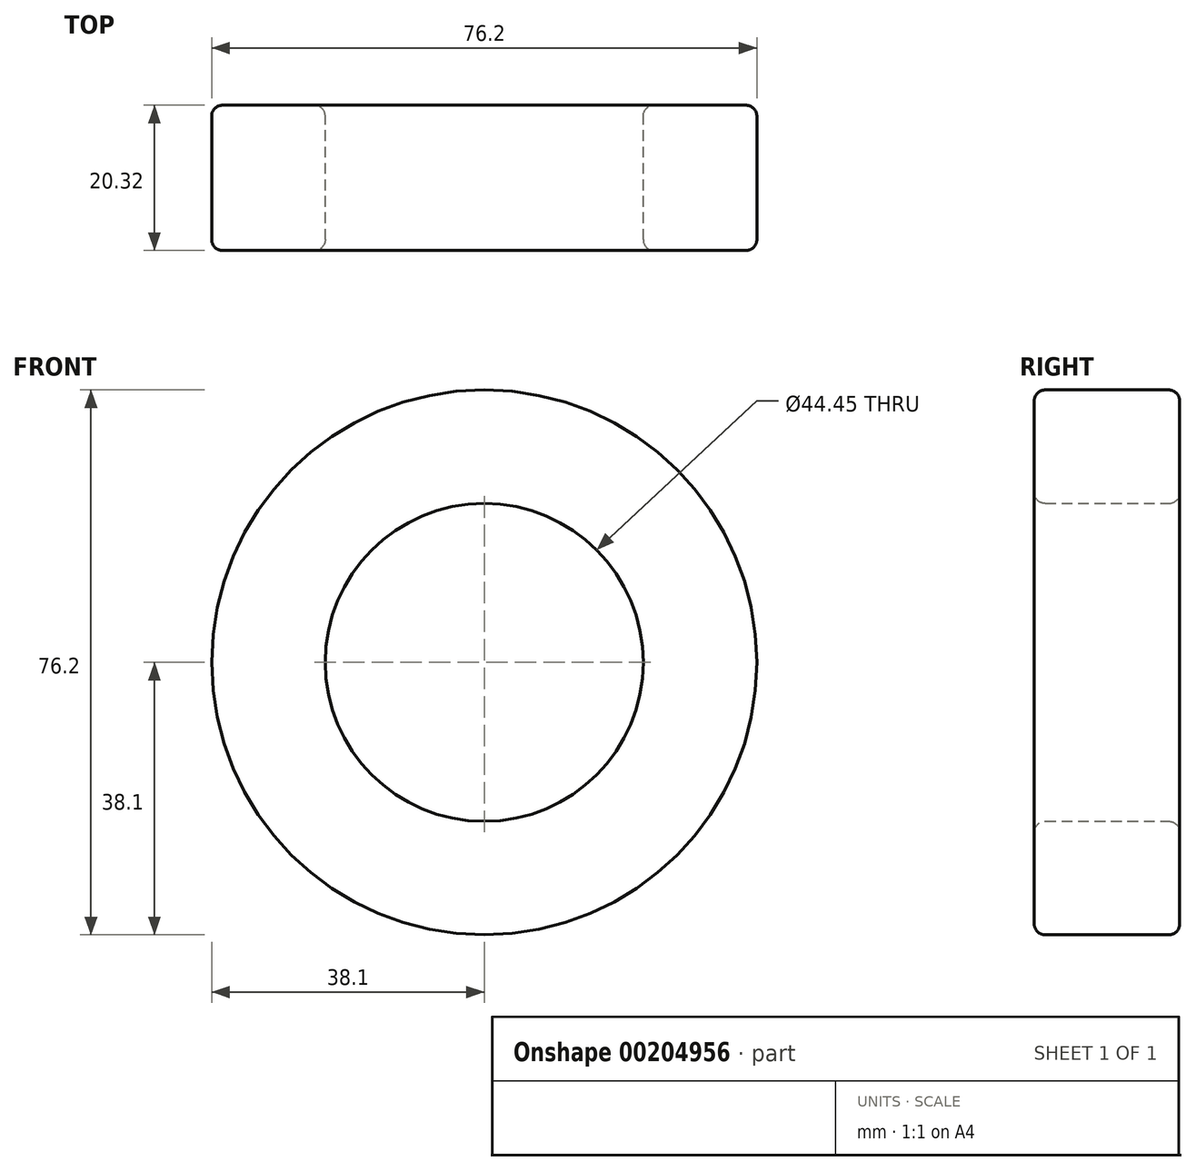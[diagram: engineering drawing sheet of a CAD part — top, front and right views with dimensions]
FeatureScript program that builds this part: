
annotation { "Feature Type Name" : "Feature", "Feature Type Description" : "" }
export const myFeature = defineFeature(function(context is Context, id is Id, definition is map)
    precondition{}
    {
        {
            var Q0;
            Q0=qCreatedBy(makeId("Front.planeOp"),FACE);
            var sketch = newSketch(context, id + "F0", { "sketchPlane" : qUnion([Q0])});
            skCircle(sketch, "E0", {"center": v(0, 0) * mm, "radius": 38.1 * mm});
            skCircle(sketch, "E1", {"center": v(0, 0) * mm, "radius": 22.23 * mm});
            skSolve(sketch);
        }
        {
            var Q0;
            Q0=makeQuery(id+"F0.imprint","IMPRINT",FACE,{"disambiguationData":[TD([[makeQuery(id+"F0.imprint","IMPRINT",EDGE,{"derivedFrom":sQuery(id+"F0.wireOp",EDGE,"E0")}),1.0]])]});
            extrude(context, id + "F1", {"entities" : qUnion([Q0]), "depth" : 20.32 * mm});
        }
        {
            var Q0;
            Q0=makeQuery(id+"F1.opExtrude","SWEPT_FACE",FACE,{"disambiguationData":[OSD([sQuery(id+"F0.wireOp",EDGE,"E0")])]});
            fillet(context, id + "F2", {"entities" : qUnion([Q0]), "radius" : 1.52 * mm, "tangentPropagation" : true, "allowEdgeOverflow" : false});
        }
        {
            var Q0;
            Q0=makeQuery(id+"F1.opExtrude","CAP_EDGE",EDGE,{"disambiguationData":[OSD([sQuery(id+"F0.wireOp",EDGE,"E1")])],"isStart":false});
            fillet(context, id + "F3", {"entities" : qUnion([Q0]), "radius" : 1.52 * mm, "tangentPropagation" : true, "allowEdgeOverflow" : false});
        }
        {
            var Q0;
            Q0=makeQuery(id+"F1.opExtrude","CAP_EDGE",EDGE,{"disambiguationData":[OSD([sQuery(id+"F0.wireOp",EDGE,"E1")])],"isStart":true});
            fillet(context, id + "F4", {"entities" : qUnion([Q0]), "radius" : 1.52 * mm, "tangentPropagation" : true, "allowEdgeOverflow" : false});
        }
    });
